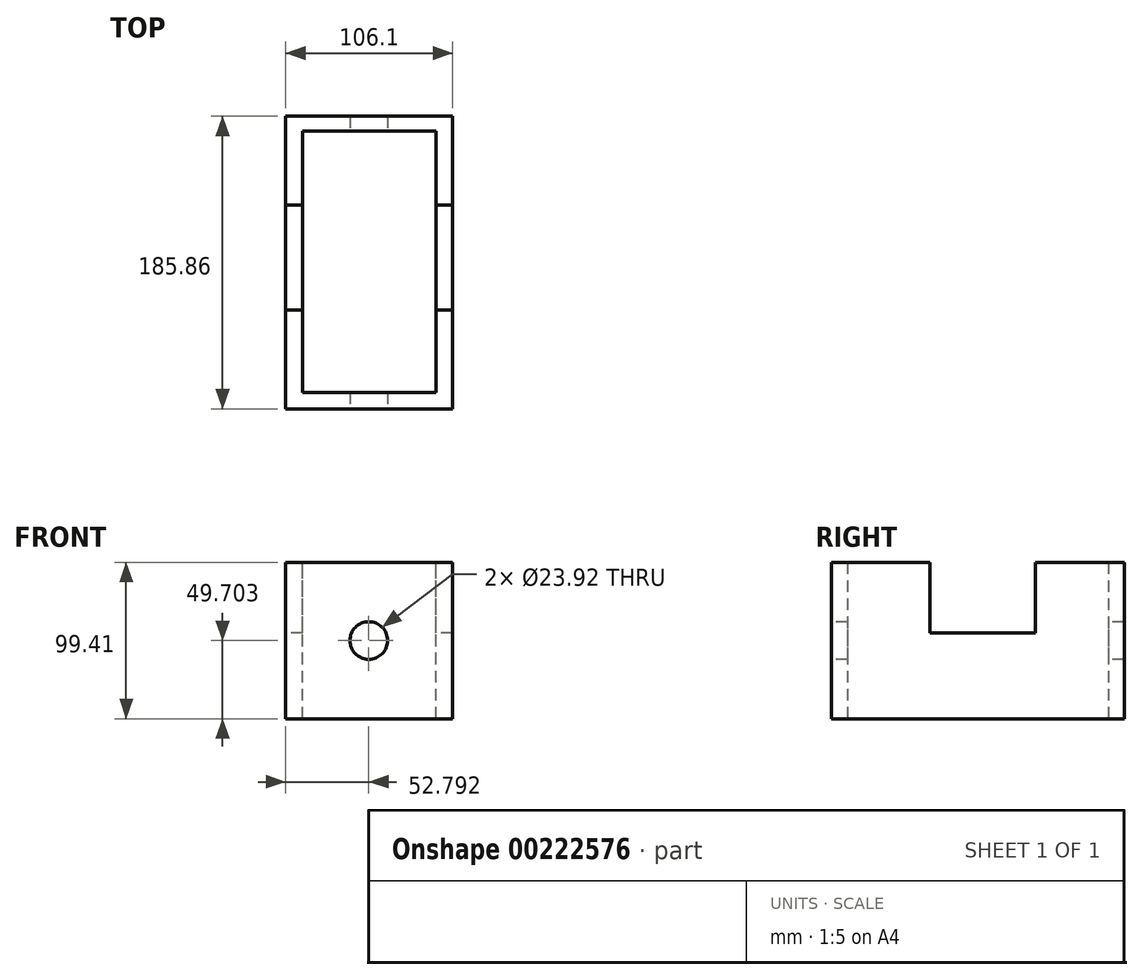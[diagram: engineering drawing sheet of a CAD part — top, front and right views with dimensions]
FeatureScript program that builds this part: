
annotation { "Feature Type Name" : "Feature", "Feature Type Description" : "" }
export const myFeature = defineFeature(function(context is Context, id is Id, definition is map)
    precondition{}
    {
        {
            var Q0;
            Q0=qCreatedBy(makeId("Top.planeOp"),FACE);
            var sketch = newSketch(context, id + "F0", { "sketchPlane" : qUnion([Q0])});
            skLineSegment(sketch, "E0.bottom", {"start": v(17.68, -92.93) * mm, "end": v(-88.42, -92.93) * mm});
            skLineSegment(sketch, "E0.top", {"start": v(17.68, 92.93) * mm, "end": v(-88.42, 92.93) * mm});
            skLineSegment(sketch, "E0.left", {"start": v(17.68, -92.93) * mm, "end": v(17.68, 92.93) * mm});
            skLineSegment(sketch, "E0.right", {"start": v(-88.42, -92.93) * mm, "end": v(-88.42, 92.93) * mm});
            skPoint(sketch, "E0.middle", {"position": v(-35.37, 0) * mm});
            skSolve(sketch);
        }
        {
            var Q0;
            Q0 = qSketchRegion(id + "F0", true);
            extrude(context, id + "F1", {"entities" : qUnion([Q0]), "depth" : 99.4 * mm});
        }
        {
            var Q0;
            Q0=makeQuery(id+"F1.opExtrude","SWEPT_FACE",FACE,{"disambiguationData":[OSD([sQuery(id+"F0.wireOp",EDGE,"E0.bottom")])]});
            var sketch = newSketch(context, id + "F2", { "sketchPlane" : qUnion([Q0])});
            skCircle(sketch, "E1", {"center": v(-35.63, 49.7) * mm, "radius": 11.96 * mm});
            skPoint(sketch, "E1.centerSnap0", {"position": v(-88.42, 49.7) * mm});
            skSolve(sketch);
        }
        {
            var Q0;
            Q0 = qSketchRegion(id + "F2", true);
            extrude(context, id + "F3", {"entities" : qUnion([Q0]), "operationType" : NewBodyOperationType.REMOVE, "endBound" : BoundingType.THROUGH_ALL, "oppositeDirection" : true, "depth" : 25.4 * mm});
        }
        {
            var Q0;
            Q0=makeQuery(id+"F1.opExtrude","SWEPT_FACE",FACE,{"disambiguationData":[OSD([sQuery(id+"F0.wireOp",EDGE,"E0.right")])]});
            var sketch = newSketch(context, id + "F4", { "sketchPlane" : qUnion([Q0])});
            skLineSegment(sketch, "E2.bottom", {"start": v(-36.45, 99.4) * mm, "end": v(30.37, 99.4) * mm});
            skLineSegment(sketch, "E2.top", {"start": v(-36.45, 54.53) * mm, "end": v(30.37, 54.53) * mm});
            skLineSegment(sketch, "E2.left", {"start": v(-36.45, 99.4) * mm, "end": v(-36.45, 54.53) * mm});
            skLineSegment(sketch, "E2.right", {"start": v(30.37, 99.4) * mm, "end": v(30.37, 54.53) * mm});
            skSolve(sketch);
        }
        {
            var Q0;
            Q0 = qSketchRegion(id + "F4", true);
            extrude(context, id + "F5", {"entities" : qUnion([Q0]), "operationType" : NewBodyOperationType.REMOVE, "endBound" : BoundingType.THROUGH_ALL, "oppositeDirection" : true, "depth" : 25.4 * mm});
        }
        {
            var Q0;
            {var subQ0=sQuery(id+"F0.wireOp",EDGE,"E0.top");var subQ1=sQuery(id+"F0.wireOp",EDGE,"E0.left");var subQ2=sQuery(id+"F0.wireOp",EDGE,"E0.right");Q0=makeQuery(id+"F5.boolean.opBoolean","SPLIT",FACE,{"disambiguationData":[TD([makeQuery(id+"F1.opExtrude","SWEPT_FACE",FACE,{"disambiguationData":[OSD([subQ0])]})])],"derivedFrom":makeQuery(id+"F1.opExtrude","CAP_FACE",FACE,{"disambiguationData":[OSD([sQuery(id+"F0.wireOp",EDGE,"E0.bottom"),subQ0,subQ1,subQ2])],"isStart":false})});}
            var sketch = newSketch(context, id + "F6", { "sketchPlane" : qUnion([Q0])});
            skLineSegment(sketch, "E3.bottom", {"start": v(-77.62, 83.36) * mm, "end": v(7.2, 83.36) * mm});
            skLineSegment(sketch, "E3.top", {"start": v(-77.62, -82.53) * mm, "end": v(7.2, -82.53) * mm});
            skLineSegment(sketch, "E3.left", {"start": v(-77.62, 83.36) * mm, "end": v(-77.62, -82.53) * mm});
            skLineSegment(sketch, "E3.right", {"start": v(7.2, 83.36) * mm, "end": v(7.2, -82.53) * mm});
            skSolve(sketch);
        }
        {
            var Q0;
            Q0 = qSketchRegion(id + "F6", true);
            extrude(context, id + "F7", {"entities" : qUnion([Q0]), "operationType" : NewBodyOperationType.REMOVE, "endBound" : BoundingType.THROUGH_ALL, "oppositeDirection" : true, "depth" : 25.4 * mm});
        }
    });
